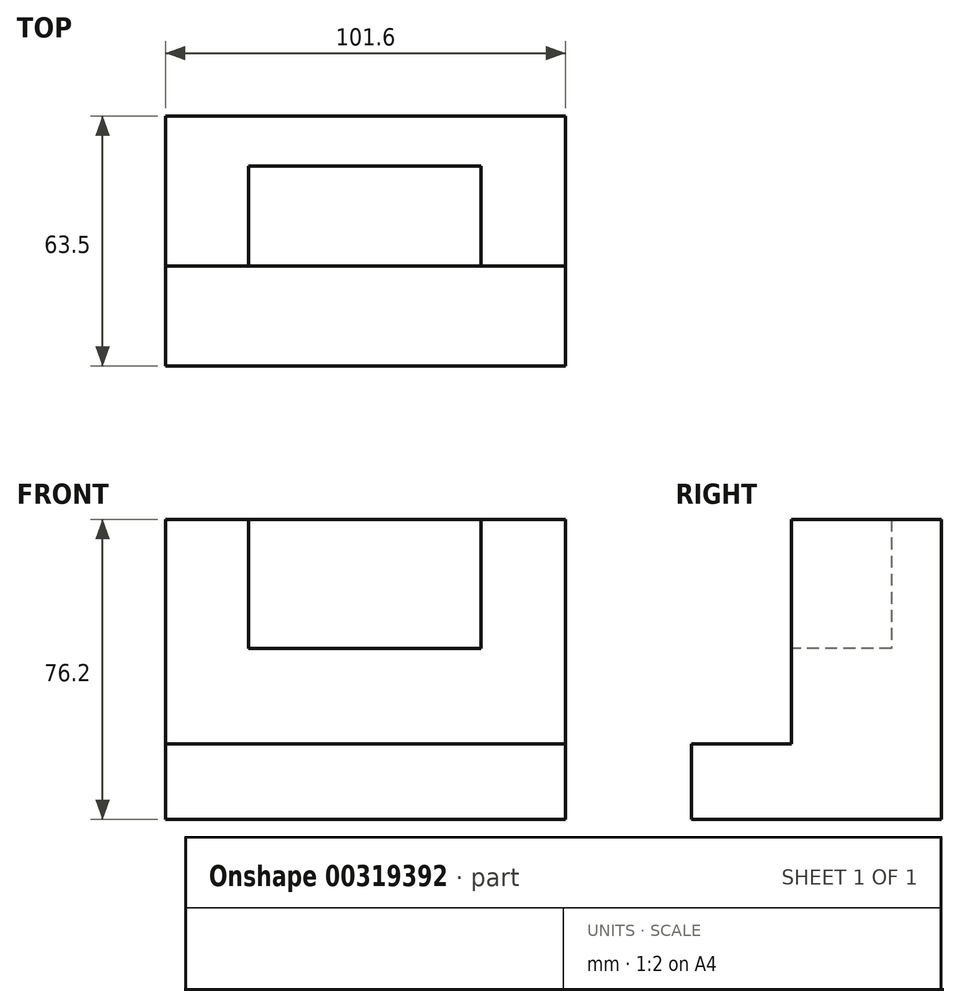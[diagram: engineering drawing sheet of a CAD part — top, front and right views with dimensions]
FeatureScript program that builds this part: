
annotation { "Feature Type Name" : "Feature", "Feature Type Description" : "" }
export const myFeature = defineFeature(function(context is Context, id is Id, definition is map)
    precondition{}
    {
        {
            var Q0;
            Q0=qCreatedBy(makeId("Right.planeOp"),FACE);
            var sketch = newSketch(context, id + "F0", { "sketchPlane" : qUnion([Q0])});
            skLineSegment(sketch, "E0", {"start": v(-33.43, -33.71) * mm, "end": v(-33.43, -52.87) * mm});
            skLineSegment(sketch, "E1", {"start": v(-33.43, -52.87) * mm, "end": v(30.07, -52.87) * mm});
            skLineSegment(sketch, "E2", {"start": v(30.07, -52.87) * mm, "end": v(30.07, 23.33) * mm});
            skLineSegment(sketch, "E3", {"start": v(30.07, 23.33) * mm, "end": v(-8.03, 23.33) * mm});
            skLineSegment(sketch, "E4", {"start": v(-8.03, 23.33) * mm, "end": v(-8.03, -33.71) * mm});
            skLineSegment(sketch, "E5", {"start": v(-8.03, -33.71) * mm, "end": v(-33.43, -33.71) * mm});
            skSolve(sketch);
        }
        {
            var Q0;
            Q0=makeQuery(id+"F0.imprint","IMPRINT",FACE,{"disambiguationData":[TD([[makeQuery(id+"F0.imprint","IMPRINT",EDGE,{"derivedFrom":sQuery(id+"F0.wireOp",EDGE,"E0")}),1.0]])]});
            extrude(context, id + "F1", {"entities" : qUnion([Q0]), "depth" : 101.6 * mm});
        }
        {
            var Q0;
            Q0=makeQuery(id+"F1.opExtrude","SWEPT_FACE",FACE,{"disambiguationData":[OSD([sQuery(id+"F0.wireOp",EDGE,"E4")])]});
            var sketch = newSketch(context, id + "F2", { "sketchPlane" : qUnion([Q0])});
            skLineSegment(sketch, "E6", {"start": v(21.06, 23.33) * mm, "end": v(21.06, -9.44) * mm});
            skLineSegment(sketch, "E7", {"start": v(21.06, -9.44) * mm, "end": v(80.17, -9.44) * mm});
            skLineSegment(sketch, "E8", {"start": v(80.17, -9.44) * mm, "end": v(80.17, 23.33) * mm});
            skSolve(sketch);
        }
        {
            var Q0;
            {var subQ0=sQuery(id+"F2.wireOp",EDGE,"E6");Q0=makeQuery(id+"F2.imprint","IMPRINT",FACE,{"disambiguationData":[TD([[makeQuery(id+"F2.imprint","IMPRINT",EDGE,{"derivedFrom":subQ0}),1.0]])]});}
            extrude(context, id + "F3", {"entities" : qUnion([Q0]), "operationType" : NewBodyOperationType.REMOVE, "oppositeDirection" : true, "depth" : 25.4 * mm});
        }
    });
